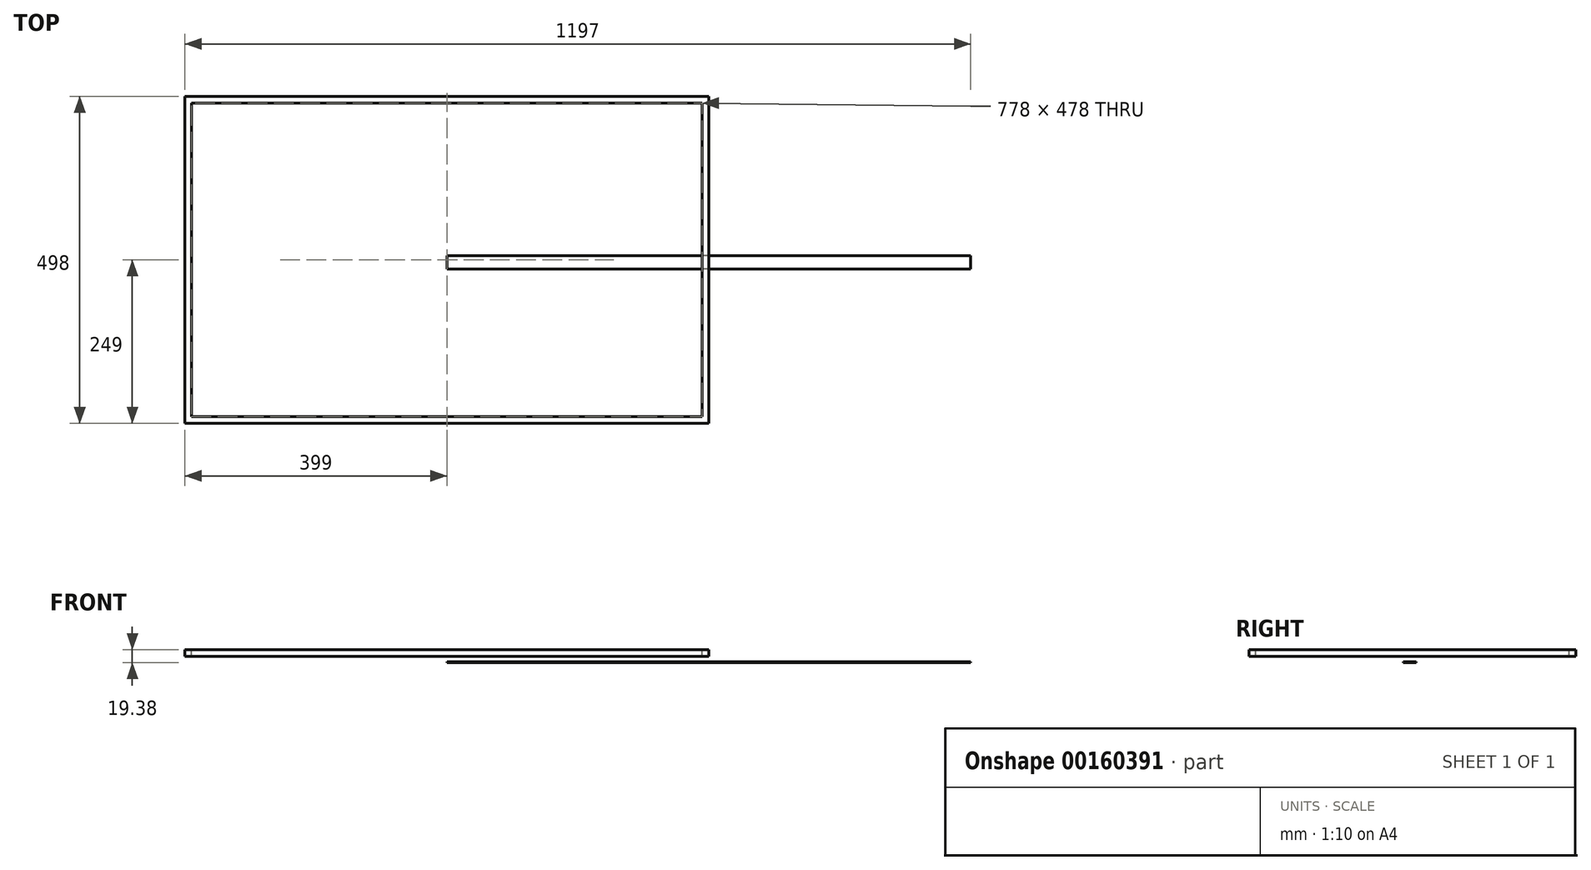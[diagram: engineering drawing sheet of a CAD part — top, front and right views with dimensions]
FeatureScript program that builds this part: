
annotation { "Feature Type Name" : "Feature", "Feature Type Description" : "" }
export const myFeature = defineFeature(function(context is Context, id is Id, definition is map)
    precondition{}
    {
        {
            var Q0;
            Q0=qCreatedBy(makeId("Top.planeOp"),FACE);
            var sketch = newSketch(context, id + "F0", { "sketchPlane" : qUnion([Q0])});
            skLineSegment(sketch, "E0.bottom", {"start": v(399, 249) * mm, "end": v(-399, 249) * mm});
            skLineSegment(sketch, "E0.top", {"start": v(399, -249) * mm, "end": v(-399, -249) * mm});
            skLineSegment(sketch, "E0.left", {"start": v(399, 249) * mm, "end": v(399, -249) * mm});
            skLineSegment(sketch, "E0.right", {"start": v(-399, 249) * mm, "end": v(-399, -249) * mm});
            skPoint(sketch, "E0.middle", {"position": v(0, 0) * mm});
            skSolve(sketch);
        }
        {
            var Q0;
            Q0=makeQuery(id+"F0.imprint","IMPRINT",FACE,{"disambiguationData":[TD([[makeQuery(id+"F0.imprint","IMPRINT",EDGE,{"derivedFrom":sQuery(id+"F0.wireOp",EDGE,"E0.bottom")}),1.0]])]});
            extrude(context, id + "F1", {"entities" : qUnion([Q0]), "depth" : 10 * mm});
        }
        {
            var Q0;
            Q0=makeQuery(id+"F1.opExtrude","CAP_FACE",FACE,{"disambiguationData":[OSD([sQuery(id+"F0.wireOp",EDGE,"E0.bottom"),sQuery(id+"F0.wireOp",EDGE,"E0.top"),sQuery(id+"F0.wireOp",EDGE,"E0.left"),sQuery(id+"F0.wireOp",EDGE,"E0.right")])],"isStart":false});
            var sketch = newSketch(context, id + "F2", { "sketchPlane" : qUnion([Q0])});
            skLineSegment(sketch, "E1.bottom", {"start": v(389, 239) * mm, "end": v(-389, 239) * mm});
            skLineSegment(sketch, "E1.top", {"start": v(389, -239) * mm, "end": v(-389, -239) * mm});
            skLineSegment(sketch, "E1.left", {"start": v(389, 239) * mm, "end": v(389, -239) * mm});
            skLineSegment(sketch, "E1.right", {"start": v(-389, 239) * mm, "end": v(-389, -239) * mm});
            skPoint(sketch, "E1.middle", {"position": v(0, 0) * mm});
            skSolve(sketch);
        }
        {
            var Q0;
            Q0=makeQuery(id+"F2.imprint","IMPRINT",FACE,{"disambiguationData":[TD([[makeQuery(id+"F2.imprint","IMPRINT",EDGE,{"derivedFrom":sQuery(id+"F2.wireOp",EDGE,"E1.bottom")}),1.0]])]});
            extrude(context, id + "F3", {"entities" : qUnion([Q0]), "operationType" : NewBodyOperationType.REMOVE, "endBound" : BoundingType.THROUGH_ALL, "oppositeDirection" : true, "depth" : 25 * mm});
        }
        {
            var Q0;
            Q0=qCreatedBy(makeId("Right.planeOp"),FACE);
            var sketch = newSketch(context, id + "F4", { "sketchPlane" : qUnion([Q0])});
            skLineSegment(sketch, "E2.bottom", {"start": v(6.08, -9.38) * mm, "end": v(-13.92, -9.38) * mm});
            skLineSegment(sketch, "E2.top", {"start": v(6.08, -8.38) * mm, "end": v(-13.92, -8.38) * mm});
            skLineSegment(sketch, "E2.left", {"start": v(6.08, -9.38) * mm, "end": v(6.08, -8.38) * mm});
            skLineSegment(sketch, "E2.right", {"start": v(-13.92, -9.38) * mm, "end": v(-13.92, -8.38) * mm});
            skSolve(sketch);
        }
        {
            var Q0;
            Q0 = qSketchRegion(id + "F4", true);
            extrude(context, id + "F5", {"entities" : qUnion([Q0]), "depth" : 798 * mm});
        }
    });
